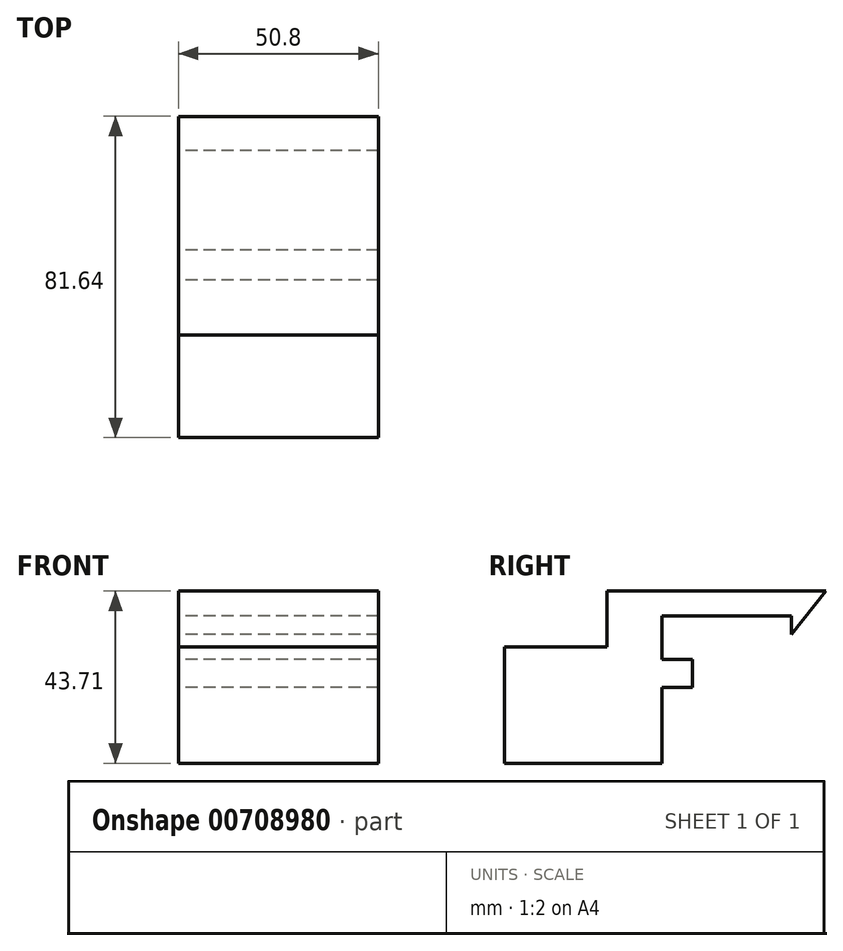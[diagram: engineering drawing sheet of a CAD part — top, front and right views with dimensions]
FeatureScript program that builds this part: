
annotation { "Feature Type Name" : "Feature", "Feature Type Description" : "" }
export const myFeature = defineFeature(function(context is Context, id is Id, definition is map)
    precondition{}
    {
        {
            var Q0;
            Q0=qCreatedBy(makeId("Right.planeOp"),FACE);
            var sketch = newSketch(context, id + "F0", { "sketchPlane" : qUnion([Q0])});
            skLineSegment(sketch, "E0", {"start": v(41.57, 43.7) * mm, "end": v(-14.04, 43.7) * mm});
            skLineSegment(sketch, "E1", {"start": v(-14.04, 43.7) * mm, "end": v(-14.04, 29.51) * mm});
            skLineSegment(sketch, "E2", {"start": v(-14.04, 29.51) * mm, "end": v(-40.07, 29.51) * mm});
            skLineSegment(sketch, "E3", {"start": v(-40.07, 29.51) * mm, "end": v(-40.07, 0) * mm});
            skLineSegment(sketch, "E4", {"start": v(-40.07, 0) * mm, "end": v(0, 0) * mm});
            skLineSegment(sketch, "E5", {"start": v(0, 0) * mm, "end": v(0, 19.26) * mm});
            skLineSegment(sketch, "E6", {"start": v(0, 19.26) * mm, "end": v(7.65, 19.26) * mm});
            skLineSegment(sketch, "E7", {"start": v(7.65, 19.26) * mm, "end": v(7.65, 26.36) * mm});
            skLineSegment(sketch, "E8", {"start": v(7.65, 26.36) * mm, "end": v(0, 26.36) * mm});
            skLineSegment(sketch, "E9", {"start": v(0, 26.36) * mm, "end": v(0, 37.4) * mm});
            skLineSegment(sketch, "E10", {"start": v(0, 37.4) * mm, "end": v(32.9, 37.4) * mm});
            skLineSegment(sketch, "E11", {"start": v(32.9, 37.4) * mm, "end": v(32.9, 32.67) * mm});
            skLineSegment(sketch, "E12", {"start": v(32.9, 32.67) * mm, "end": v(41.57, 43.7) * mm});
            skSolve(sketch);
        }
        {
            var Q0;
            Q0 = qSketchRegion(id + "F0", true);
            extrude(context, id + "F1", {"entities" : qUnion([Q0]), "depth" : 50.8 * mm, "offsetDistance" : 25.4 * mm});
        }
    });
